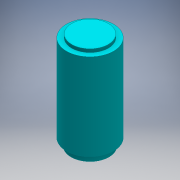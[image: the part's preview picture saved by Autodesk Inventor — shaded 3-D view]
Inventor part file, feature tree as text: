
AUTODESK INVENTOR PART (.ipt)
format: ipt  version: 2016 (Build 200138000, 138)  size: 116,224 bytes
history: native  units: mm
features: extrude x3, sketch x3
ambient origin geometry x8: Origin, YZ Plane, XZ Plane, XY Plane, X Axis, Y Axis, Z Axis, Center Point
bodies: Solid1 (feature_tree)
feature tree (6):
  extrude  "Extrusion1"  Depth=5.0mm TaperAngle=0.0deg
  extrude  "Extrusion2"  Depth=59.3mm TaperAngle=0.0deg
  extrude  "Extrusion3"  Depth=2.2mm TaperAngle=0.0deg
  sketch  "Sketch1"  dims[d0=26.0mm d1=5.0mm d2=0.0mm]
  sketch  "Sketch2"  dims[d3=32.2mm d4=59.3mm d5=0.0mm]
  sketch  "Sketch3"  dims[d6=25.0mm d7=2.2mm d8=0.0mm]
